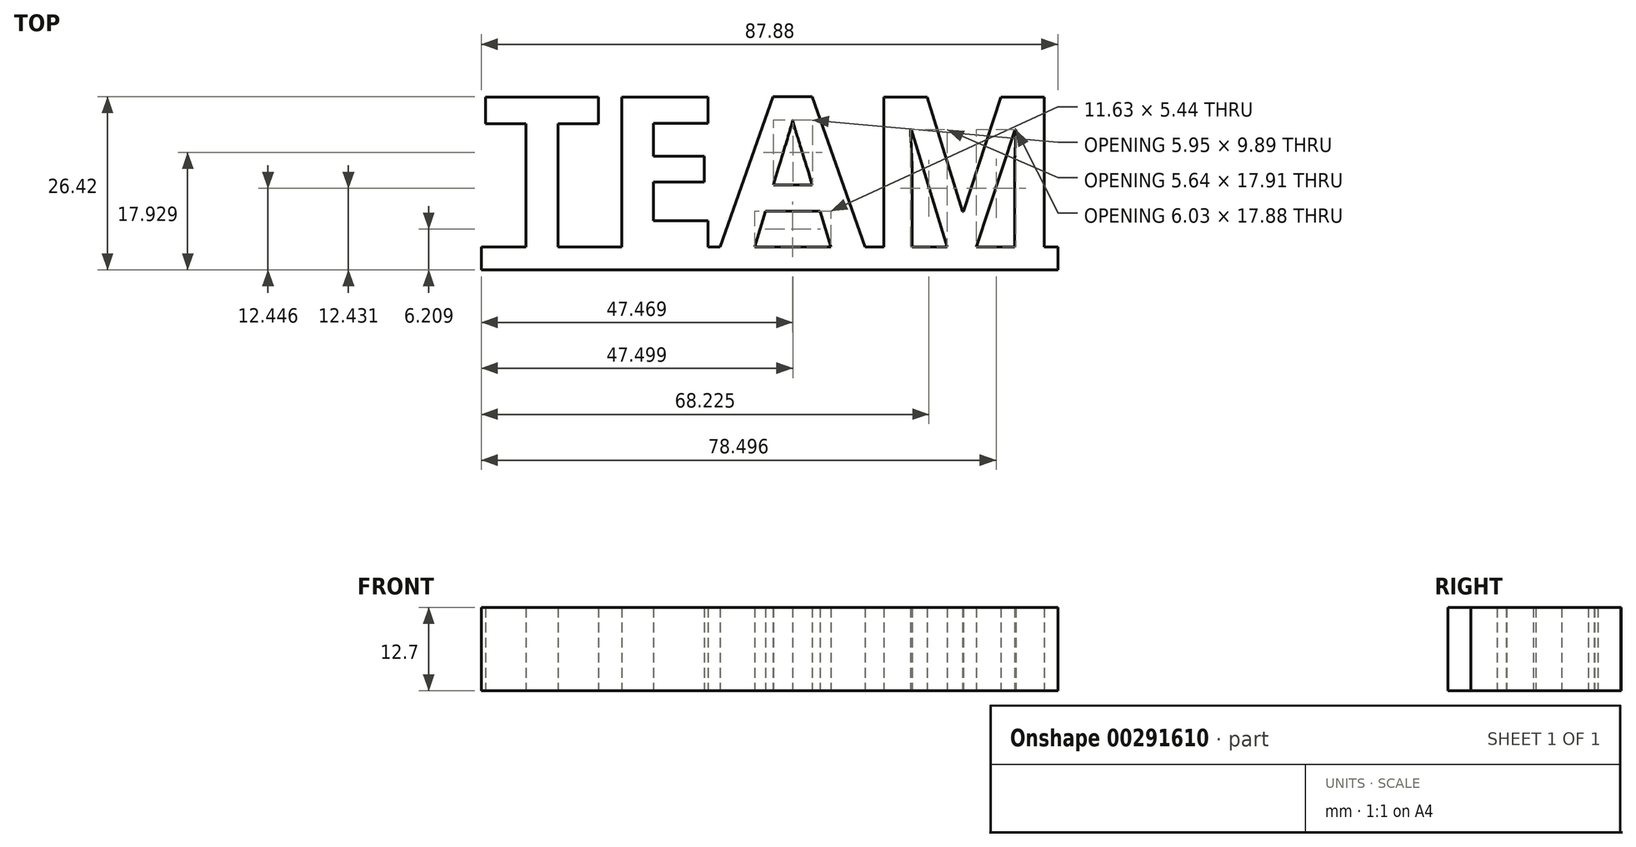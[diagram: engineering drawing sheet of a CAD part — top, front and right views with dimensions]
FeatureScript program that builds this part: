
annotation { "Feature Type Name" : "Feature", "Feature Type Description" : "" }
export const myFeature = defineFeature(function(context is Context, id is Id, definition is map)
    precondition{}
    {
        {
            var Q0;
            Q0=qCreatedBy(makeId("Top.planeOp"),FACE);
            var sketch = newSketch(context, id + "F0", { "sketchPlane" : qUnion([Q0])});
            skText(sketch, "E0", { "text": "TEAM", "fontName": "OpenSans-Bold.ttf"});
            skLineSegment(sketch, "E1.bottom", {"start": v(-43.92, 0) * mm, "end": v(43.96, 0) * mm});
            skLineSegment(sketch, "E1.top", {"start": v(-43.92, -3.49) * mm, "end": v(43.96, -3.49) * mm});
            skLineSegment(sketch, "E1.left", {"start": v(-43.92, 0) * mm, "end": v(-43.92, -3.49) * mm});
            skLineSegment(sketch, "E1.right", {"start": v(43.96, 0) * mm, "end": v(43.96, -3.49) * mm});
            const initialGuessF0  = {"E0": [-0.04392, 0, 1, 0, 0.02303]};
            skSetInitialGuess(sketch, initialGuessF0);
            skSolve(sketch);
        }
        {
            var Q0;
            Q0 = qSketchRegion(id + "F0", true);
            extrude(context, id + "F1", {"entities" : qUnion([Q0]), "depth" : 12.7 * mm});
        }
    });
